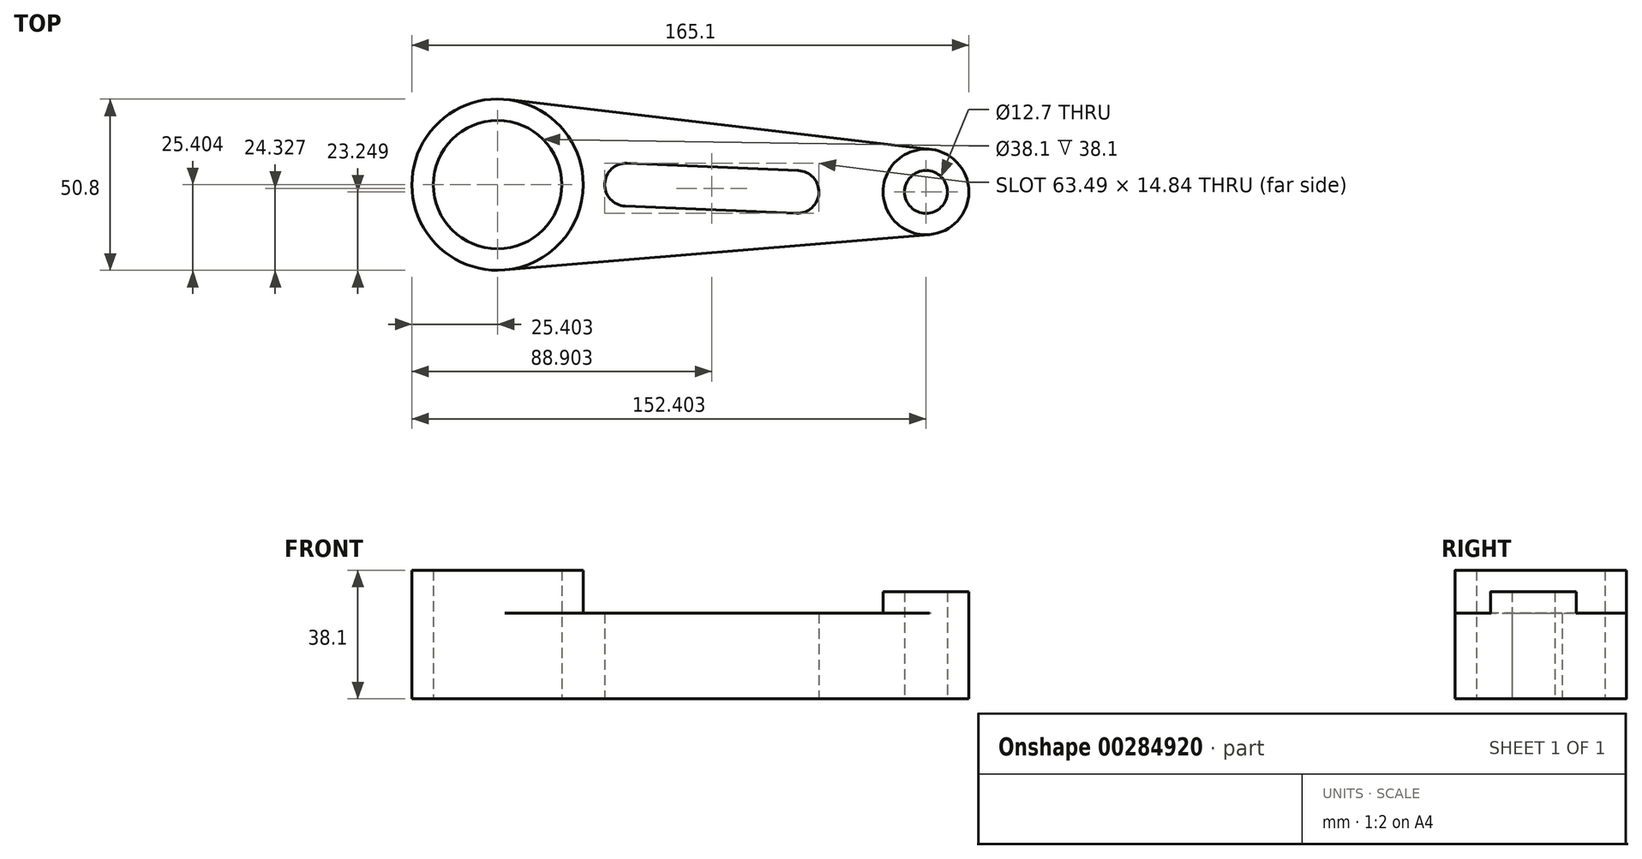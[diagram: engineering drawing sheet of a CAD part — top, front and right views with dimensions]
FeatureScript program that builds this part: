
annotation { "Feature Type Name" : "Feature", "Feature Type Description" : "" }
export const myFeature = defineFeature(function(context is Context, id is Id, definition is map)
    precondition{}
    {
        {
            var Q0;
            Q0=qCreatedBy(makeId("Top.planeOp"),FACE);
            var sketch = newSketch(context, id + "F0", { "sketchPlane" : qUnion([Q0])});
            skCircle(sketch, "E0", {"center": v(-22.7, 6.34) * mm, "radius": 25.4 * mm});
            skCircle(sketch, "E1", {"center": v(-22.7, 6.34) * mm, "radius": 19.05 * mm});
            skCircle(sketch, "E2", {"center": v(104.3, 4.19) * mm, "radius": 6.35 * mm});
            skCircle(sketch, "E3", {"center": v(104.3, 4.19) * mm, "radius": 12.7 * mm});
            skLineSegment(sketch, "E4", {"start": v(-19.74, 31.57) * mm, "end": v(105.78, 16.8) * mm});
            skLineSegment(sketch, "E5", {"start": v(105.35, -8.47) * mm, "end": v(-20.6, -18.97) * mm});
            skArc(sketch, "E6", {"start": v(15.66, 12.69) * mm, "mid": v(9.05, 6.61) * mm, "end": v(15.12, 0) * mm});
            skArc(sketch, "E7", {"start": v(65.92, -2.16) * mm, "mid": v(72.54, 3.92) * mm, "end": v(66.46, 10.53) * mm});
            skLineSegment(sketch, "E8", {"start": v(66.46, 10.53) * mm, "end": v(15.66, 12.69) * mm});
            skLineSegment(sketch, "E9", {"start": v(65.92, -2.16) * mm, "end": v(15.12, 0) * mm});
            skSolve(sketch);
        }
        {
            var Q0;
            {var subQ1=sQuery(id+"F0.wireOp",EDGE,"E4");Q0=makeQuery(id+"F0.imprint","IMPRINT",FACE,{"disambiguationData":[TD([[makeQuery(id+"F0.imprint","IMPRINT",EDGE,{"derivedFrom":subQ1}),-1.0]])]});}
            extrude(context, id + "F1", {"entities" : qUnion([Q0]), "depth" : 25.4 * mm});
        }
        {
            var Q0;
            Q0=makeQuery(id+"F0.imprint","IMPRINT",FACE,{"disambiguationData":[TD([[makeQuery(id+"F0.imprint","IMPRINT",EDGE,{"derivedFrom":sQuery(id+"F0.wireOp",EDGE,"E2")}),-1.0]])]});
            extrude(context, id + "F2", {"entities" : qUnion([Q0]), "operationType" : NewBodyOperationType.ADD, "depth" : 31.75 * mm});
        }
        {
            var Q0;
            Q0=makeQuery(id+"F0.imprint","IMPRINT",FACE,{"disambiguationData":[TD([[makeQuery(id+"F0.imprint","IMPRINT",EDGE,{"derivedFrom":sQuery(id+"F0.wireOp",EDGE,"E1")}),-1.0]])]});
            extrude(context, id + "F3", {"entities" : qUnion([Q0]), "operationType" : NewBodyOperationType.ADD, "depth" : 38.1 * mm});
        }
    });
